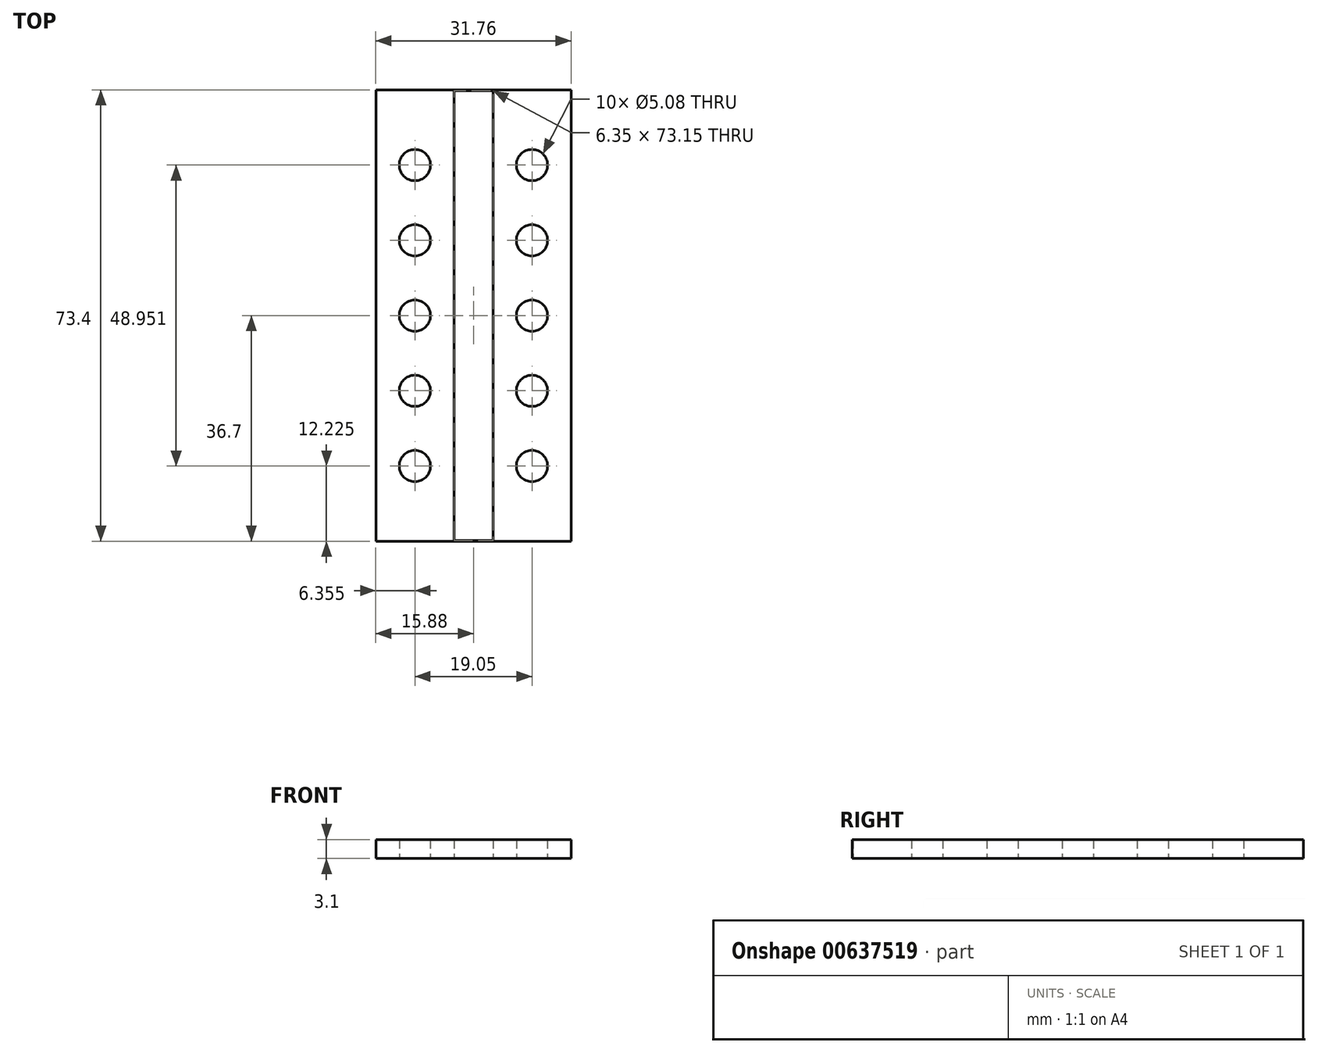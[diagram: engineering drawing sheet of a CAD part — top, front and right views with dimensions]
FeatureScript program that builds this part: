
annotation { "Feature Type Name" : "Feature", "Feature Type Description" : "" }
export const myFeature = defineFeature(function(context is Context, id is Id, definition is map)
    precondition{}
    {
        {
            var Q0;
            Q0=qCreatedBy(makeId("Top.planeOp"),FACE);
            var sketch = newSketch(context, id + "F0", { "sketchPlane" : qUnion([Q0])});
            skLineSegment(sketch, "E0.bottom", {"start": v(-15.88, 36.7) * mm, "end": v(15.88, 36.7) * mm});
            skLineSegment(sketch, "E0.top", {"start": v(-15.88, -36.7) * mm, "end": v(15.88, -36.7) * mm});
            skLineSegment(sketch, "E0.left", {"start": v(-15.88, 36.7) * mm, "end": v(-15.88, -36.7) * mm});
            skLineSegment(sketch, "E0.right", {"start": v(15.88, 36.7) * mm, "end": v(15.88, -36.7) * mm});
            skPoint(sketch, "E0.middle", {"position": v(0, 0) * mm});
            skCircle(sketch, "E1", {"center": v(-9.52, 0) * mm, "radius": 2.54 * mm});
            skCircle(sketch, "E2", {"center": v(-9.52, 12.23) * mm, "radius": 2.54 * mm});
            skCircle(sketch, "E3", {"center": v(-9.52, 24.48) * mm, "radius": 2.54 * mm});
            skCircle(sketch, "E4.MirrorC", {"center": v(-9.52, -12.23) * mm, "radius": 2.54 * mm});
            skCircle(sketch, "E5.MirrorC", {"center": v(-9.52, -24.48) * mm, "radius": 2.54 * mm});
            skCircle(sketch, "E6.MirrorC", {"center": v(9.52, 24.48) * mm, "radius": 2.54 * mm});
            skCircle(sketch, "E7.MirrorC", {"center": v(9.52, 12.23) * mm, "radius": 2.54 * mm});
            skCircle(sketch, "E8.MirrorC", {"center": v(9.52, 0) * mm, "radius": 2.54 * mm});
            skCircle(sketch, "E9.MirrorC", {"center": v(9.52, -12.23) * mm, "radius": 2.54 * mm});
            skCircle(sketch, "E10.MirrorC", {"center": v(9.52, -24.48) * mm, "radius": 2.54 * mm});
            skLineSegment(sketch, "E11.bottom", {"start": v(-3.1, 36.7) * mm, "end": v(3.18, 36.7) * mm});
            skLineSegment(sketch, "E11.top", {"start": v(-3.17, -36.7) * mm, "end": v(3.1, -36.7) * mm});
            skLineSegment(sketch, "E12.top", {"start": v(-3.18, -36.7) * mm, "end": v(3.1, -36.7) * mm});
            skLineSegment(sketch, "E13.bottom", {"start": v(-3.17, 36.7) * mm, "end": v(3.18, 36.7) * mm});
            skLineSegment(sketch, "E13.top", {"start": v(-3.24, -36.7) * mm, "end": v(3.1, -36.7) * mm});
            skLineSegment(sketch, "E14.bottom", {"start": v(3.17, 36.58) * mm, "end": v(-3.18, 36.58) * mm});
            skLineSegment(sketch, "E14.top", {"start": v(3.18, -36.58) * mm, "end": v(-3.17, -36.58) * mm});
            skLineSegment(sketch, "E14.left", {"start": v(3.17, 36.58) * mm, "end": v(3.18, -36.58) * mm});
            skLineSegment(sketch, "E14.right", {"start": v(-3.18, 36.58) * mm, "end": v(-3.17, -36.58) * mm});
            skSolve(sketch);
        }
        {
            var Q0;
            Q0 = qSketchRegion(id + "F0", true);
            extrude(context, id + "F1", {"entities" : qUnion([Q0]), "endBound" : BoundingType.SYMMETRIC, "depth" : 3.1 * mm, "offsetDistance" : 25.4 * mm});
        }
    });
